# Revit family: 0047647 Feilo Sylvania Lighting Fixtures START FLAT HE 600 4000K DALI G2
name_source: partatom
category: Lighting Fixtures
revit_build: Autodesk Revit 2017 (Build: 20190507_1515(x64)
units: mm (PartAtom-declared; Revit-internal decimal feet)

## family parameters
Cut with Voids When Loaded = No
Host = Face
Light Source = Yes
OmniClass Number = 23.80.70.11.17
OmniClass Title = Specialized Lighting by Location or Use
Part Type = Normal
Room Calculation Point = No
Round Connector Dimension = Use Diameter
Shared = No

## types (1)
- 0047647 START FLAT HE 600 4000K DALI G2
    Apparent Load = 36 VA
    Assembly Code = D5020200
    AssetType = Fixed
    BodyMaterial = Metal_Sylvania_Startflat Panel LED_White
    Color Filter = 16777215
    Cutout Length = 574 mm  [stored 1.8832 ft]
    Cutout Width = 574 mm  [stored 1.8832 ft]
    Default Elevation = 0 mm  [stored 0 ft]
    Description = Ultra thin LED Panel, excellent uniformity of light, perfect for ceilings with low voids, high efficacy.Ulta thin edgelit LED 600x600mm Panel with, excellent uniform light distribution. Acrylic PMMA diffuser optimising light output whilst reducing glare. 4239lm 93lm/W.
    DiffuserMaterial = Polycarbonate_Sylvania_Startflat Panel LED_Opal
    Dimming Lamp Color Temperature Shift = <None>
    DimmingControlOptions = Dimmable
    DocumentationLiterature = http://www.sylvania-lighting.com
    DurationUnit = hours
    ElectricShockClassification = Class II
    Emit Shape Visible in Rendering = No
    Emit from Rectangle Length = 545 mm  [stored 1.78806 ft]
    Emit from Rectangle Width = 545 mm  [stored 1.78806 ft]
    ExpectedLife = 50000
    IfcExportAs = IfcLightFixtureType
    IfcExportType = IfcLightFixtureType
    ImpactProtectionIndex = IK03
    IngressProtection = IP20
    InputNominalFrequency = 50/60 Hz
    InputVoltage = 220-240V~
    Keynote = 16500
    Lamp = Integrated LED
    LampColourRenderingIndex = 80
    LampColourTemperature = 4000 K
    LampMacAdamStep = 6
    LampNominalLuminous = 4200 lm
    LampsType = Integrated LED
    LuminousEfficacy = 120 lm/W
    Manufacturer = Feilo-Sylvania Group
    ManufacturerName = Feilo Sylvania
    Material = aluminium housing, pmma diffuser
    Model = START FLAT HE 600 4000K DALI G2
    ModelNumber = 0047647
    ModelReference = START FLAT HE 600 4000K DALI G2
    MountingMaterial = Metal_Sylvania_Startflat Panel LED_Silver
    Name = START FLAT HE 600 4000K DALI G2
    NominalHeight = 10.5 mm  [stored 0.0344488 ft]
    NominalLength = 595 mm  [stored 1.9521 ft]
    NominalWidth = 0 mm  [stored 0 ft]
    Photometric Web File = 0047647.ies
    PowerConsumption = 36 W
    PowerFactor = 0.98
    Tilt Angle = -90.00°
    TypeName = START FLAT HE 600 4000K DALI G2
    URL = http://www.sylvania-lighting.com
    Voltage = 230 V
    Weight = 12.25 kg

note: [stored X ft] marks values corroborated as IEEE doubles in the binary element streams (Revit-internal decimal feet)

## geometry (parser evidence)
native form markers: Sweep x2
no freeform markers — native parametric forms only
